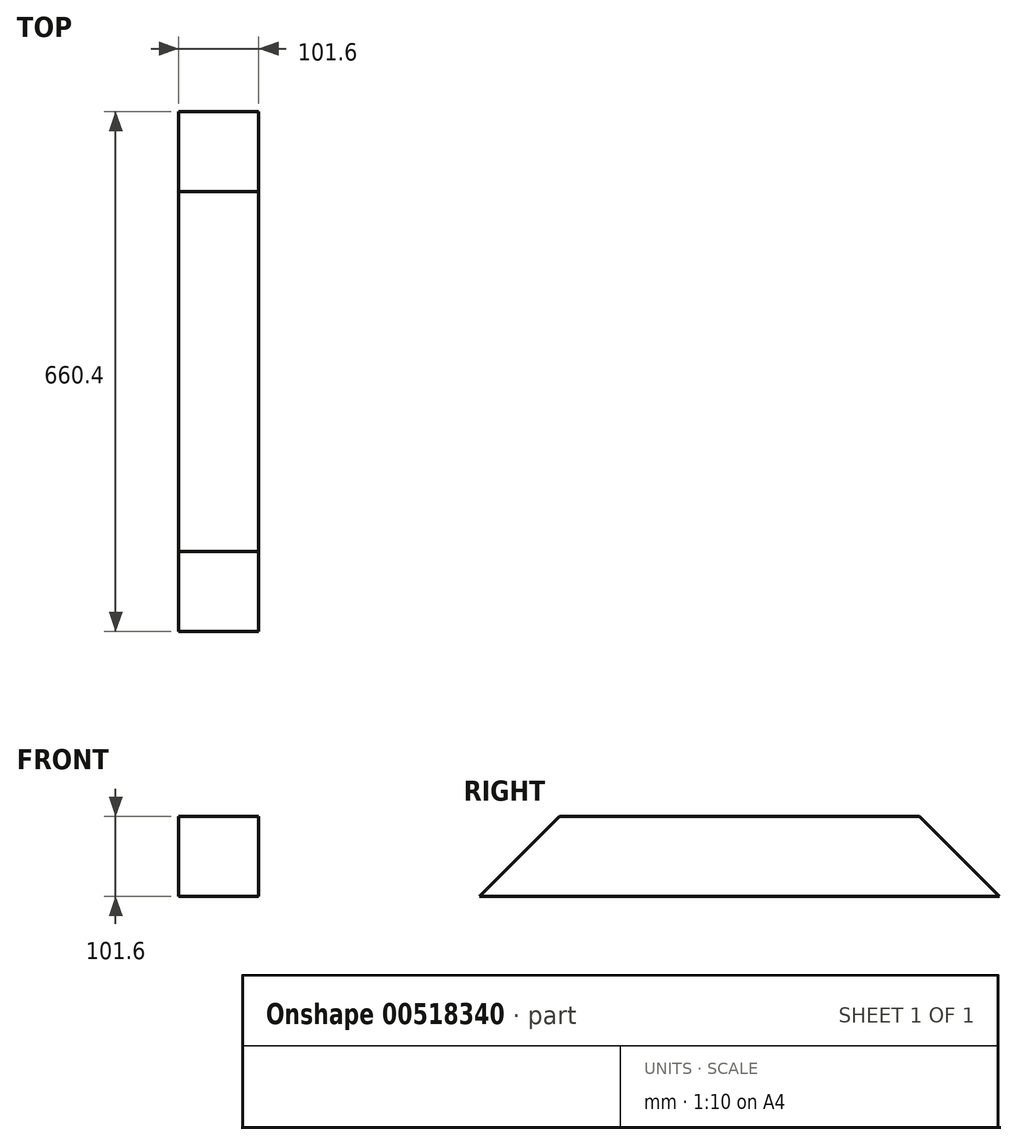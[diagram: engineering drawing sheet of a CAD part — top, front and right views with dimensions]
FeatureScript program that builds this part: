
annotation { "Feature Type Name" : "Feature", "Feature Type Description" : "" }
export const myFeature = defineFeature(function(context is Context, id is Id, definition is map)
    precondition{}
    {
        {
            var Q0;
            Q0=qCreatedBy(makeId("Top.planeOp"),FACE);
            var sketch = newSketch(context, id + "F0", { "sketchPlane" : qUnion([Q0])});
            skLineSegment(sketch, "E0.bottom", {"start": v(-50.8, 330.2) * mm, "end": v(50.8, 330.2) * mm});
            skLineSegment(sketch, "E0.top", {"start": v(-50.8, -330.2) * mm, "end": v(50.8, -330.2) * mm});
            skLineSegment(sketch, "E0.left", {"start": v(-50.8, 330.2) * mm, "end": v(-50.8, -330.2) * mm});
            skLineSegment(sketch, "E0.right", {"start": v(50.8, 330.2) * mm, "end": v(50.8, -330.2) * mm});
            skPoint(sketch, "E0.middle", {"position": v(0, 0) * mm});
            skSolve(sketch);
        }
        {
            var Q0;
            Q0 = qSketchRegion(id + "F0", true);
            extrude(context, id + "F1", {"entities" : qUnion([Q0]), "depth" : 101.6 * mm, "offsetDistance" : 25.4 * mm});
        }
        {
            var Q0;
            Q0=makeQuery(id+"F1.opExtrude","SWEPT_FACE",FACE,{"disambiguationData":[OSD([sQuery(id+"F0.wireOp",EDGE,"E0.right")])]});
            var sketch = newSketch(context, id + "F2", { "sketchPlane" : qUnion([Q0])});
            skLineSegment(sketch, "E1", {"start": v(-330.2, 0) * mm, "end": v(-228.6, 101.6) * mm});
            skLineSegment(sketch, "E2", {"start": v(-228.6, 101.6) * mm, "end": v(-330.2, 101.6) * mm});
            skLineSegment(sketch, "E3", {"start": v(-330.2, 101.6) * mm, "end": v(-330.2, 0) * mm});
            skLineSegment(sketch, "E4", {"start": v(330.2, 0) * mm, "end": v(228.6, 101.6) * mm});
            skLineSegment(sketch, "E5", {"start": v(228.6, 101.6) * mm, "end": v(330.2, 101.6) * mm});
            skLineSegment(sketch, "E6", {"start": v(330.2, 101.6) * mm, "end": v(330.2, 0) * mm});
            skSolve(sketch);
        }
        {
            var Q0;
            Q0 = qSketchRegion(id + "F2", true);
            extrude(context, id + "F3", {"entities" : qUnion([Q0]), "operationType" : NewBodyOperationType.REMOVE, "oppositeDirection" : true, "depth" : 101.6 * mm, "offsetDistance" : 25.4 * mm});
        }
    });
